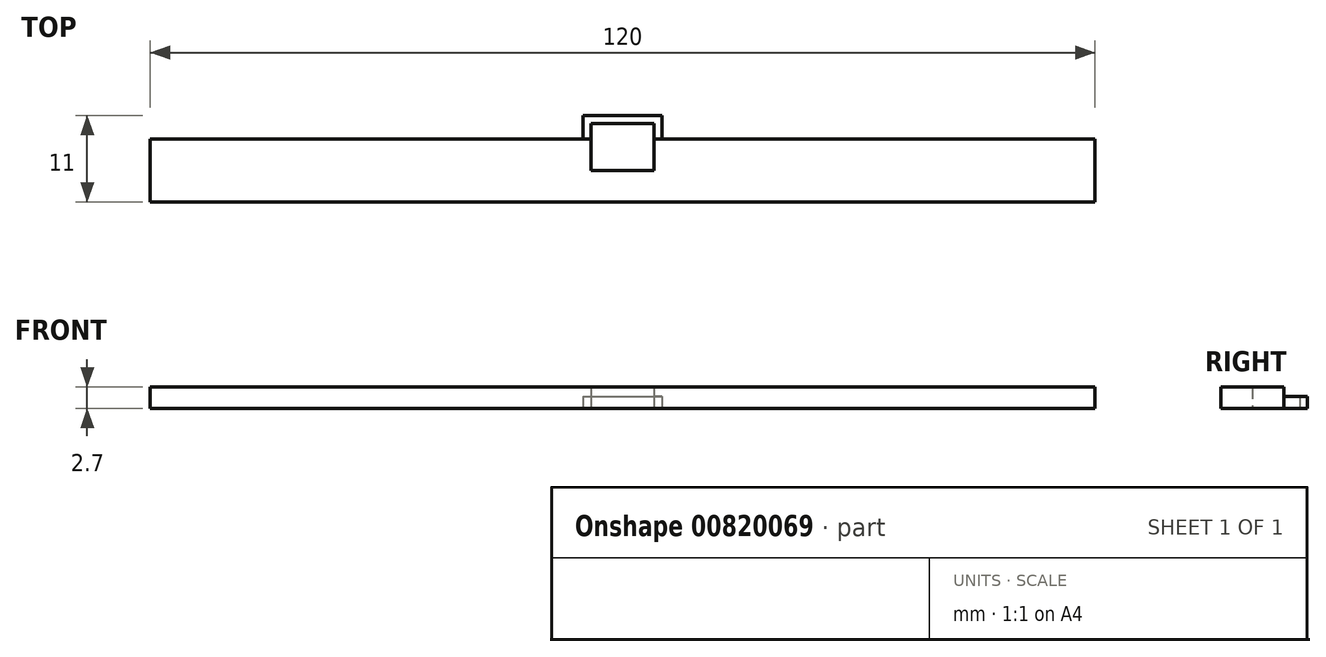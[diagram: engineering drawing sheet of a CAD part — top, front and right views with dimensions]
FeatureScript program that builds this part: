
annotation { "Feature Type Name" : "Feature", "Feature Type Description" : "" }
export const myFeature = defineFeature(function(context is Context, id is Id, definition is map)
    precondition{}
    {
        {
            var Q0;
            Q0=qCreatedBy(makeId("Top.planeOp"),FACE);
            var sketch = newSketch(context, id + "F0", { "sketchPlane" : qUnion([Q0])});
            skLineSegment(sketch, "E0", {"start": v(0, 0) * mm, "end": v(120, 0) * mm});
            skLineSegment(sketch, "E1", {"start": v(120, 0) * mm, "end": v(120, 8) * mm});
            skLineSegment(sketch, "E2", {"start": v(120, 8) * mm, "end": v(0, 8) * mm});
            skLineSegment(sketch, "E3", {"start": v(0, 8) * mm, "end": v(0, 0) * mm});
            skLineSegment(sketch, "E4", {"start": v(60, 8) * mm, "end": v(60, 0) * mm, "construction": true});
            skLineSegment(sketch, "E5", {"start": v(56, 8) * mm, "end": v(56, 4) * mm});
            skLineSegment(sketch, "E6", {"start": v(56, 4) * mm, "end": v(64, 4) * mm});
            skLineSegment(sketch, "E7", {"start": v(64, 4) * mm, "end": v(64, 8) * mm});
            skLineSegment(sketch, "E8", {"start": v(56, 8) * mm, "end": v(56, 10) * mm});
            skLineSegment(sketch, "E9", {"start": v(56, 10) * mm, "end": v(64, 10) * mm});
            skLineSegment(sketch, "E10", {"start": v(64, 10) * mm, "end": v(64, 8) * mm});
            skLineSegment(sketch, "E11.bottom", {"start": v(55, 8) * mm, "end": v(65, 8) * mm});
            skLineSegment(sketch, "E11.top", {"start": v(55, 11) * mm, "end": v(65, 11) * mm});
            skLineSegment(sketch, "E11.left", {"start": v(55, 8) * mm, "end": v(55, 11) * mm});
            skLineSegment(sketch, "E11.right", {"start": v(65, 8) * mm, "end": v(65, 11) * mm});
            skSolve(sketch);
        }
        {
            var Q0;
            Q0=makeQuery(id+"F0.imprint","IMPRINT",FACE,{"disambiguationData":[TD([[makeQuery(id+"F0.imprint","IMPRINT",EDGE,{"derivedFrom":sQuery(id+"F0.wireOp",EDGE,"E0")}),1.0]])]});
            var Q1;
            {var subQ1=sQuery(id+"F0.wireOp",EDGE,"E8");Q1=makeQuery(id+"F0.imprint","IMPRINT",FACE,{"disambiguationData":[TD([[makeQuery(id+"F0.imprint","IMPRINT",EDGE,{"derivedFrom":subQ1}),1.0]])]});}
            extrude(context, id + "F1", {"entities" : qUnion([Q0, Q1]), "depth" : 1.5 * mm, "offsetDistance" : 25 * mm});
        }
        {
            var Q0;
            Q0=makeQuery(id+"F1.opExtrude","CAP_FACE",FACE,{"disambiguationData":[OSD([sQuery(id+"F0.wireOp",EDGE,"E0"),sQuery(id+"F0.wireOp",EDGE,"E1"),sQuery(id+"F0.wireOp",EDGE,"E2"),sQuery(id+"F0.wireOp",EDGE,"E3"),sQuery(id+"F0.wireOp",EDGE,"E5"),sQuery(id+"F0.wireOp",EDGE,"E6"),sQuery(id+"F0.wireOp",EDGE,"E7"),sQuery(id+"F0.wireOp",EDGE,"E8"),sQuery(id+"F0.wireOp",EDGE,"E9"),sQuery(id+"F0.wireOp",EDGE,"E10"),sQuery(id+"F0.wireOp",EDGE,"E11.top"),sQuery(id+"F0.wireOp",EDGE,"E11.left"),sQuery(id+"F0.wireOp",EDGE,"E11.right")])],"isStart":false});
            var sketch = newSketch(context, id + "F2", { "sketchPlane" : qUnion([Q0])});
            skLineSegment(sketch, "E12", {"start": v(0, 0) * mm, "end": v(0, 8) * mm});
            skLineSegment(sketch, "E13", {"start": v(0, 8) * mm, "end": v(56, 8) * mm});
            skLineSegment(sketch, "E14", {"start": v(56, 8) * mm, "end": v(56, 4) * mm});
            skLineSegment(sketch, "E15", {"start": v(56, 4) * mm, "end": v(64, 4) * mm});
            skLineSegment(sketch, "E16", {"start": v(64, 4) * mm, "end": v(64, 8) * mm});
            skLineSegment(sketch, "E17", {"start": v(64, 8) * mm, "end": v(120, 8) * mm});
            skLineSegment(sketch, "E18", {"start": v(120, 8) * mm, "end": v(120, 0) * mm});
            skLineSegment(sketch, "E19", {"start": v(120, 0) * mm, "end": v(0, 0) * mm});
            skSolve(sketch);
        }
        {
            var Q0;
            {var subQ3=sQuery(id+"F2.wireOp",EDGE,"E12");Q0=makeQuery(id+"F2.imprint","IMPRINT",FACE,{"disambiguationData":[TD([[makeQuery(id+"F2.imprint","IMPRINT",EDGE,{"derivedFrom":subQ3}),1.0]])]});}
            extrude(context, id + "F3", {"entities" : qUnion([Q0]), "operationType" : NewBodyOperationType.ADD, "depth" : 1.2 * mm, "offsetDistance" : 25 * mm});
        }
    });
